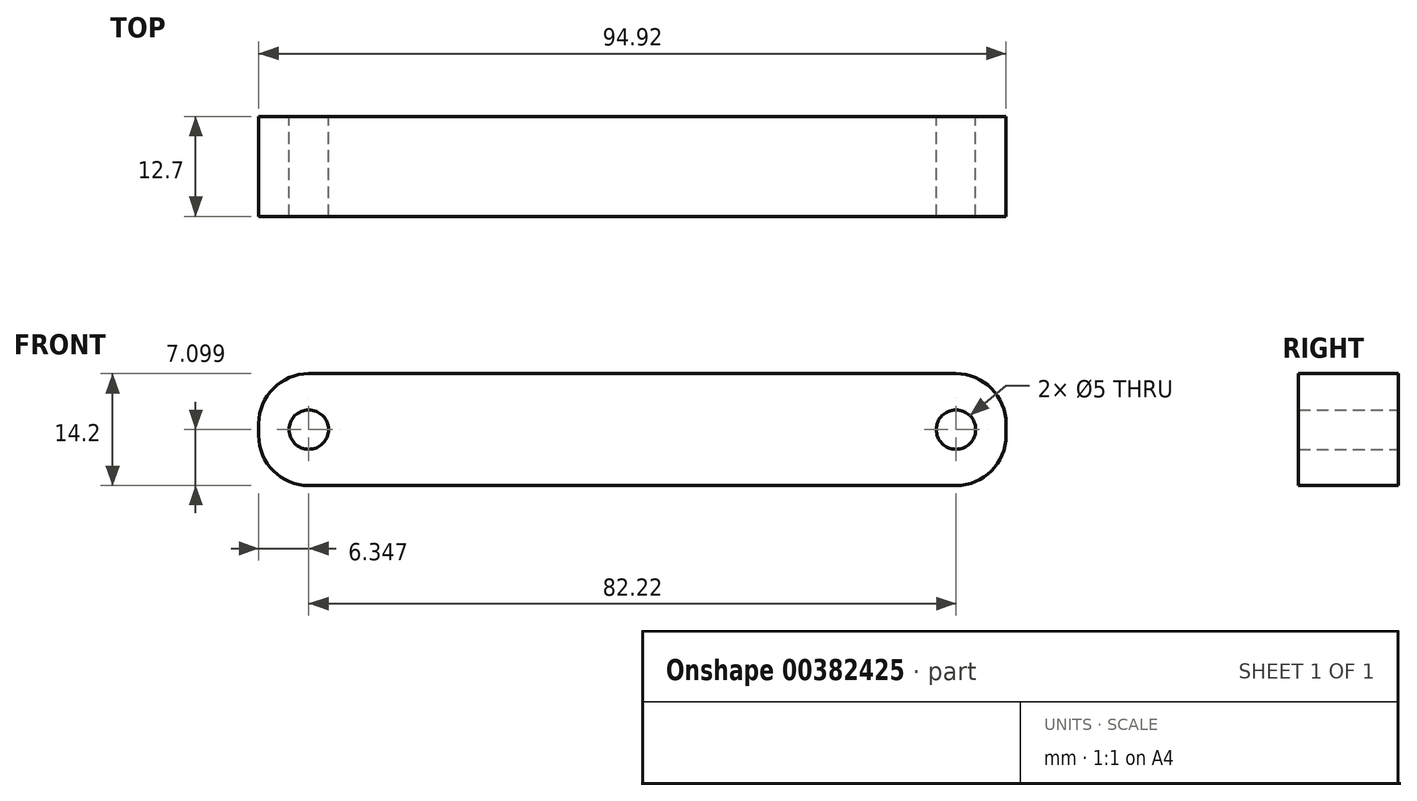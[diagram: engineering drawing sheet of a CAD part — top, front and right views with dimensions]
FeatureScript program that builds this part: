
annotation { "Feature Type Name" : "Feature", "Feature Type Description" : "" }
export const myFeature = defineFeature(function(context is Context, id is Id, definition is map)
    precondition{}
    {
        {
            var Q0;
            Q0=qCreatedBy(makeId("Front.planeOp"),FACE);
            var sketch = newSketch(context, id + "F0", { "sketchPlane" : qUnion([Q0])});
            skLineSegment(sketch, "E0", {"start": v(29.62, 0) * mm, "end": v(-52.6, 0) * mm});
            skLineSegment(sketch, "E1", {"start": v(-58.95, -6.35) * mm, "end": v(-58.95, -7.85) * mm});
            skLineSegment(sketch, "E2", {"start": v(-52.6, -14.2) * mm, "end": v(29.62, -14.2) * mm});
            skLineSegment(sketch, "E3", {"start": v(35.97, -7.85) * mm, "end": v(35.97, -6.35) * mm});
            skPoint(sketch, "E4.visualSharp", {"position": v(-58.95, 0) * mm});
            skArc(sketch, "E4.filletArc", {"start": v(-52.6, 0) * mm, "mid": v(-57.1, -1.86) * mm, "end": v(-58.95, -6.35) * mm});
            skPoint(sketch, "E5.visualSharp", {"position": v(-58.95, -14.2) * mm});
            skArc(sketch, "E5.filletArc", {"start": v(-58.95, -7.85) * mm, "mid": v(-57.1, -12.34) * mm, "end": v(-52.6, -14.2) * mm});
            skPoint(sketch, "E6.visualSharp", {"position": v(35.97, -14.2) * mm});
            skArc(sketch, "E6.filletArc", {"start": v(29.62, -14.2) * mm, "mid": v(34.1, -12.34) * mm, "end": v(35.97, -7.85) * mm});
            skPoint(sketch, "E7.visualSharp", {"position": v(35.97, 0) * mm});
            skArc(sketch, "E7.filletArc", {"start": v(35.97, -6.35) * mm, "mid": v(34.1, -1.86) * mm, "end": v(29.62, 0) * mm});
            skCircle(sketch, "E8", {"center": v(-52.6, -7.1) * mm, "radius": 2.5 * mm});
            skPoint(sketch, "E8.centerSnap0", {"position": v(-58.95, -7.1) * mm});
            skCircle(sketch, "E9", {"center": v(29.62, -7.1) * mm, "radius": 2.5 * mm});
            skPoint(sketch, "E9.centerSnap0", {"position": v(35.97, -7.1) * mm});
            skSolve(sketch);
        }
        {
            var Q0;
            Q0 = qSketchRegion(id + "F0", true);
            extrude(context, id + "F1", {"entities" : qUnion([Q0]), "depth" : 12.7 * mm});
        }
    });
